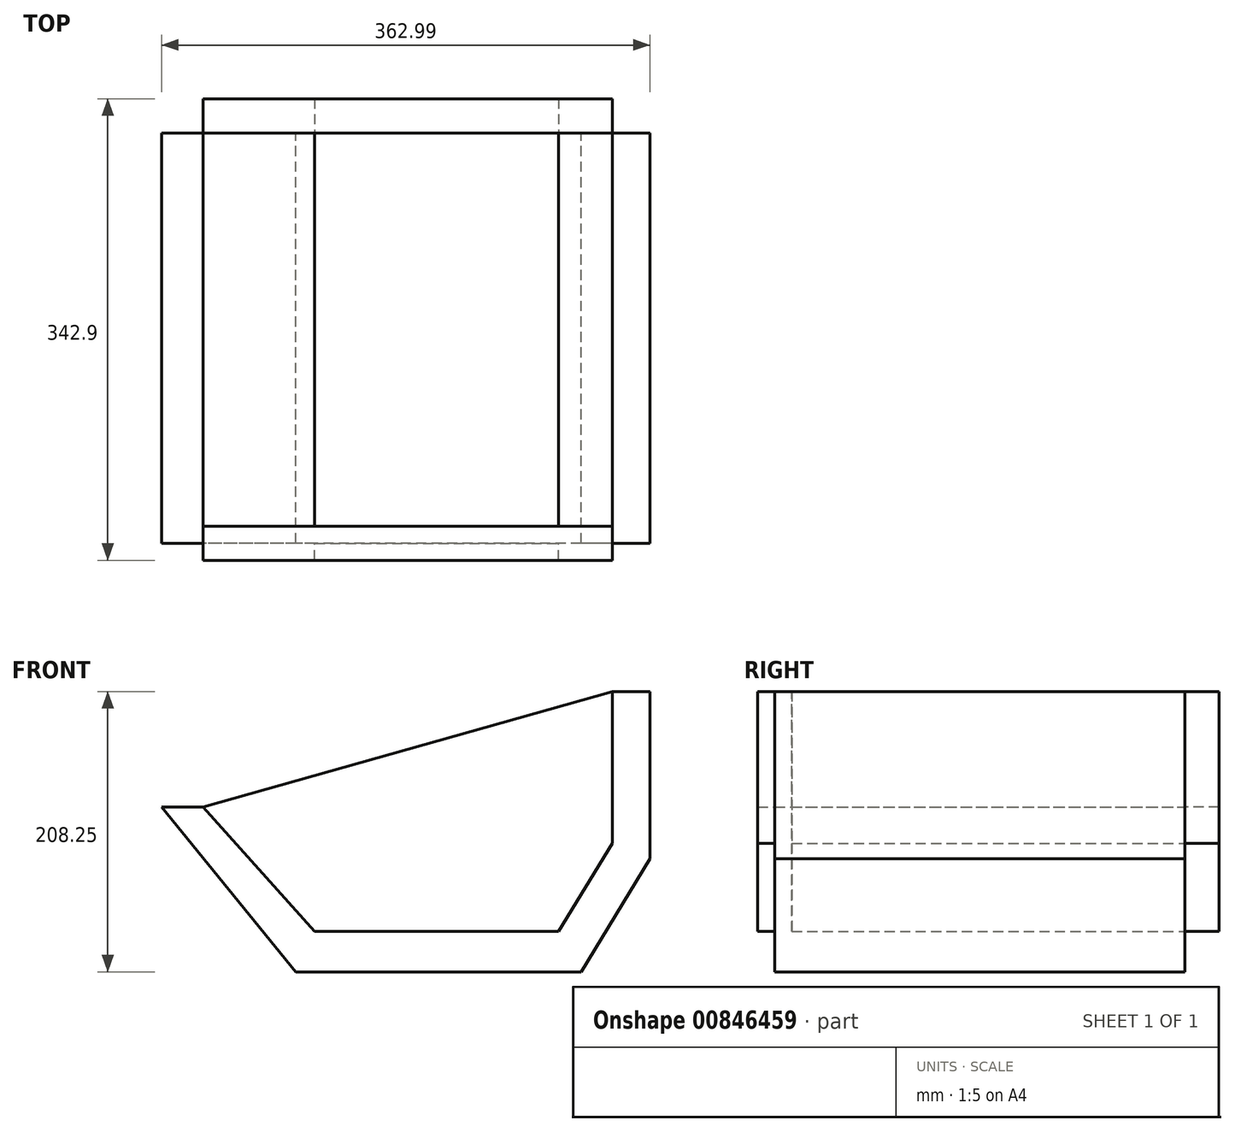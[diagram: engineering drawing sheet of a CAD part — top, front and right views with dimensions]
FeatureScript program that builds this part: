
annotation { "Feature Type Name" : "Feature", "Feature Type Description" : "" }
export const myFeature = defineFeature(function(context is Context, id is Id, definition is map)
    precondition{}
    {
        {
            var Q0;
            Q0=qCreatedBy(makeId("Front.planeOp"),FACE);
            var sketch = newSketch(context, id + "F0", { "sketchPlane" : qUnion([Q0])});
            skLineSegment(sketch, "E0.top", {"start": v(-32.32, -28.67) * mm, "end": v(85.25, -28.67) * mm});
            skLineSegment(sketch, "E1", {"start": v(-32.32, -28.67) * mm, "end": v(-95.82, -28.67) * mm});
            skLineSegment(sketch, "E2", {"start": v(-95.82, -28.67) * mm, "end": v(-178.97, 63.68) * mm});
            skLineSegment(sketch, "E3", {"start": v(125.29, 36.89) * mm, "end": v(85.25, -28.67) * mm});
            skLineSegment(sketch, "E4", {"start": v(125.29, 149.6) * mm, "end": v(125.29, 36.89) * mm});
            skLineSegment(sketch, "E5.0", {"start": v(153.32, 149.6) * mm, "end": v(125.29, 149.6) * mm});
            skLineSegment(sketch, "E5.1", {"start": v(153.32, 149.6) * mm, "end": v(153.32, 25.28) * mm});
            skLineSegment(sketch, "E5.3", {"start": v(153.32, 25.28) * mm, "end": v(102.06, -58.65) * mm});
            skLineSegment(sketch, "E5.4", {"start": v(-178.97, 63.68) * mm, "end": v(-209.67, 63.68) * mm});
            skLineSegment(sketch, "E5.5", {"start": v(-110.06, -58.65) * mm, "end": v(-209.67, 63.68) * mm});
            skLineSegment(sketch, "E5.6", {"start": v(-32.32, -58.65) * mm, "end": v(-110.06, -58.65) * mm});
            skLineSegment(sketch, "E5.7", {"start": v(-32.32, -58.65) * mm, "end": v(102.06, -58.65) * mm});
            skSolve(sketch);
        }
        {
            var Q0;
            Q0=makeQuery(id+"F0.imprint","IMPRINT",FACE,{"disambiguationData":[TD([[makeQuery(id+"F0.imprint","IMPRINT",EDGE,{"derivedFrom":sQuery(id+"F0.wireOp",EDGE,"E0.top")}),-1.0]])]});
            extrude(context, id + "F1", {"entities" : qUnion([Q0]), "endBound" : BoundingType.SYMMETRIC, "depth" : 304.8 * mm, "offsetDistance" : 25.4 * mm});
        }
        {
            var Q0;
            Q0=makeQuery(id+"F1.opExtrude","CAP_FACE",FACE,{"disambiguationData":[OSD([sQuery(id+"F0.wireOp",EDGE,"E0.top"),sQuery(id+"F0.wireOp",EDGE,"E1"),sQuery(id+"F0.wireOp",EDGE,"E2"),sQuery(id+"F0.wireOp",EDGE,"E3"),sQuery(id+"F0.wireOp",EDGE,"E4"),sQuery(id+"F0.wireOp",EDGE,"E5.0"),sQuery(id+"F0.wireOp",EDGE,"E5.1"),sQuery(id+"F0.wireOp",EDGE,"E5.3"),sQuery(id+"F0.wireOp",EDGE,"E5.4"),sQuery(id+"F0.wireOp",EDGE,"E5.5"),sQuery(id+"F0.wireOp",EDGE,"E5.6"),sQuery(id+"F0.wireOp",EDGE,"E5.7")])],"isStart":false});
            var sketch = newSketch(context, id + "F2", { "sketchPlane" : qUnion([Q0])});
            skLineSegment(sketch, "E6", {"start": v(-178.97, 63.68) * mm, "end": v(125.29, 149.6) * mm});
            skSolve(sketch);
        }
        {
            var Q0;
            Q0=makeQuery(id+"F2.imprint","IMPRINT",FACE,{"disambiguationData":[TD([[makeQuery(id+"F2.imprint","IMPRINT",EDGE,{"derivedFrom":sQuery(id+"F2.wireOp",EDGE,"E6")}),-1.0]])]});
            extrude(context, id + "F3", {"entities" : qUnion([Q0]), "operationType" : NewBodyOperationType.ADD, "endBound" : BoundingType.SYMMETRIC, "depth" : 25.4 * mm, "offsetDistance" : 25.4 * mm});
        }
        {
            var Q0;
            Q0=makeQuery(id+"F1.opExtrude","CAP_FACE",FACE,{"disambiguationData":[OSD([sQuery(id+"F0.wireOp",EDGE,"E0.top"),sQuery(id+"F0.wireOp",EDGE,"E1"),sQuery(id+"F0.wireOp",EDGE,"E2"),sQuery(id+"F0.wireOp",EDGE,"E3"),sQuery(id+"F0.wireOp",EDGE,"E4"),sQuery(id+"F0.wireOp",EDGE,"E5.0"),sQuery(id+"F0.wireOp",EDGE,"E5.1"),sQuery(id+"F0.wireOp",EDGE,"E5.3"),sQuery(id+"F0.wireOp",EDGE,"E5.4"),sQuery(id+"F0.wireOp",EDGE,"E5.5"),sQuery(id+"F0.wireOp",EDGE,"E5.6"),sQuery(id+"F0.wireOp",EDGE,"E5.7")])],"isStart":true});
            var sketch = newSketch(context, id + "F4", { "sketchPlane" : qUnion([Q0])});
            skLineSegment(sketch, "E7", {"start": v(-125.29, 149.6) * mm, "end": v(178.97, 63.68) * mm});
            skSolve(sketch);
        }
        {
            var Q0;
            Q0=makeQuery(id+"F4.imprint","IMPRINT",FACE,{"disambiguationData":[TD([[makeQuery(id+"F4.imprint","IMPRINT",EDGE,{"derivedFrom":sQuery(id+"F4.wireOp",EDGE,"E7")}),-1.0]])]});
            extrude(context, id + "F5", {"entities" : qUnion([Q0]), "depth" : 25.4 * mm, "offsetDistance" : 25.4 * mm});
        }
    });
